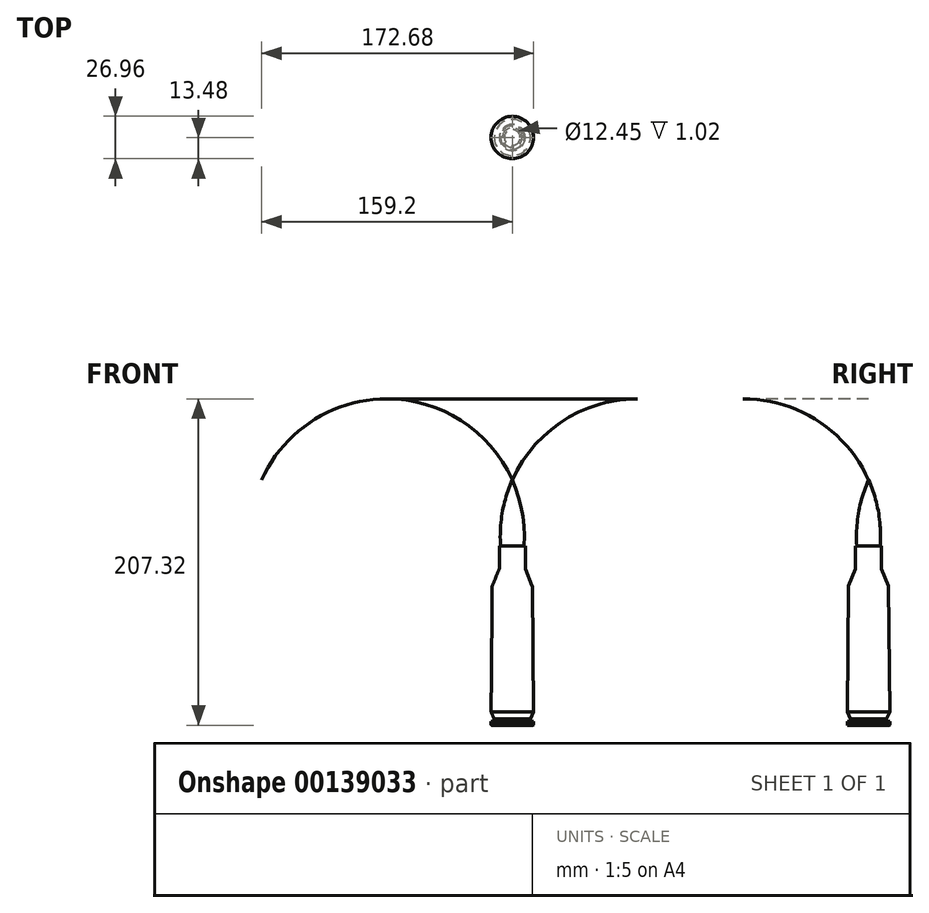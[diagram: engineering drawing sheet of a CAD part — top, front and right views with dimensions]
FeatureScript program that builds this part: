
annotation { "Feature Type Name" : "Feature", "Feature Type Description" : "" }
export const myFeature = defineFeature(function(context is Context, id is Id, definition is map)
    precondition{}
    {
        {
            var Q0;
            Q0=qCreatedBy(makeId("Front.planeOp"),FACE);
            var sketch = newSketch(context, id + "F0", { "sketchPlane" : qUnion([Q0])});
            skLineSegment(sketch, "E0", {"start": v(0, -92) * mm, "end": v(0, 75.96) * mm, "construction": true});
            skLineSegment(sketch, "E1", {"start": v(-81.81, 0) * mm, "end": v(-13.22, 0) * mm, "construction": true});
            skLineSegment(sketch, "E2", {"start": v(-13.22, 0) * mm, "end": v(-13.47, 0.25) * mm});
            skLineSegment(sketch, "E3", {"start": v(-13.47, 0.25) * mm, "end": v(-13.47, 2.5) * mm});
            skLineSegment(sketch, "E4", {"start": v(-13.47, 2.5) * mm, "end": v(-11.5, 2.5) * mm});
            skLineSegment(sketch, "E5", {"start": v(-11.5, 2.5) * mm, "end": v(-11.5, 4) * mm});
            skLineSegment(sketch, "E6", {"start": v(-11.5, 4) * mm, "end": v(-13.47, 8.5) * mm});
            skLineSegment(sketch, "E7", {"start": v(-13.47, 8.5) * mm, "end": v(-12.75, 88.37) * mm});
            skLineSegment(sketch, "E8", {"start": v(-8.25, 99.37) * mm, "end": v(-8.25, 114) * mm});
            skLineSegment(sketch, "E9", {"start": v(-8.25, 114) * mm, "end": v(-7.44, 114) * mm});
            skLineSegment(sketch, "E10", {"start": v(0, 114) * mm, "end": v(0, 0) * mm});
            skLineSegment(sketch, "E11", {"start": v(-12.75, 88.37) * mm, "end": v(-8.25, 99.37) * mm});
            skLineSegment(sketch, "E12", {"start": v(0, 114) * mm, "end": v(0, 155.8) * mm});
            skArc(sketch, "E13", {"start": v(0, 155.8) * mm, "mid": v(-6.3, 135.36) * mm, "end": v(-7.44, 114) * mm});
            skLineSegment(sketch, "E14.trimOffspring", {"start": v(0, 0) * mm, "end": v(86.14, 0) * mm, "construction": true});
            skLineSegment(sketch, "E15", {"start": v(-13.22, 0) * mm, "end": v(-6.22, 0) * mm});
            skLineSegment(sketch, "E16", {"start": v(-6.22, 0) * mm, "end": v(-6.22, 1.02) * mm});
            skLineSegment(sketch, "E17", {"start": v(-6.22, 1.02) * mm, "end": v(-5, 1.02) * mm});
            skLineSegment(sketch, "E18", {"start": v(-5, 1.02) * mm, "end": v(-5, 0) * mm});
            skLineSegment(sketch, "E19", {"start": v(-5, 0) * mm, "end": v(0, 0) * mm});
            skLineSegment(sketch, "E20", {"start": v(0, 103.22) * mm, "end": v(0, 114) * mm});
            skSolve(sketch);
        }
        {
            var Q0;
            Q0=makeQuery(id+"F0.imprint","IMPRINT",FACE,{"disambiguationData":[TD([[makeQuery(id+"F0.imprint","IMPRINT",EDGE,{"derivedFrom":sQuery(id+"F0.wireOp",EDGE,"E2")}),-1.0]])]});
            var Q1;
            Q1=sQuery(id+"F0.wireOp",EDGE,"E12");
            revolve(context, id + "F1", {"entities" : qUnion([Q0]), "axis" : qUnion([Q1]), "revolveType" : RevolveType.FULL});
        }
        {
            var Q0;
            Q0=makeQuery(id+"F1.opRevolve","SWEPT_EDGE",EDGE,{"disambiguationData":[OSD([sQuery(id+"F0.wireOp",EDGE,"E8"),sQuery(id+"F0.wireOp",EDGE,"E11")])]});
            var Q1;
            Q1=makeQuery(id+"F1.opRevolve","SWEPT_EDGE",EDGE,{"disambiguationData":[OSD([sQuery(id+"F0.wireOp",EDGE,"E7"),sQuery(id+"F0.wireOp",EDGE,"E11")])]});
            fillet(context, id + "F2", {"entities" : qUnion([Q0, Q1]), "radius" : 1 * mm, "tangentPropagation" : true, "allowEdgeOverflow" : false});
        }
        {
            var Q0;
            Q0=qCreatedBy(makeId("Right.planeOp"),FACE);
            cPlane(context, id + "F3", {"entities" : qUnion([Q0]), "cplaneType" : CPlaneType.OFFSET, "offset" : 25 * mm, "width" : 150 * mm, "height" : 150 * mm});
        }
    });
